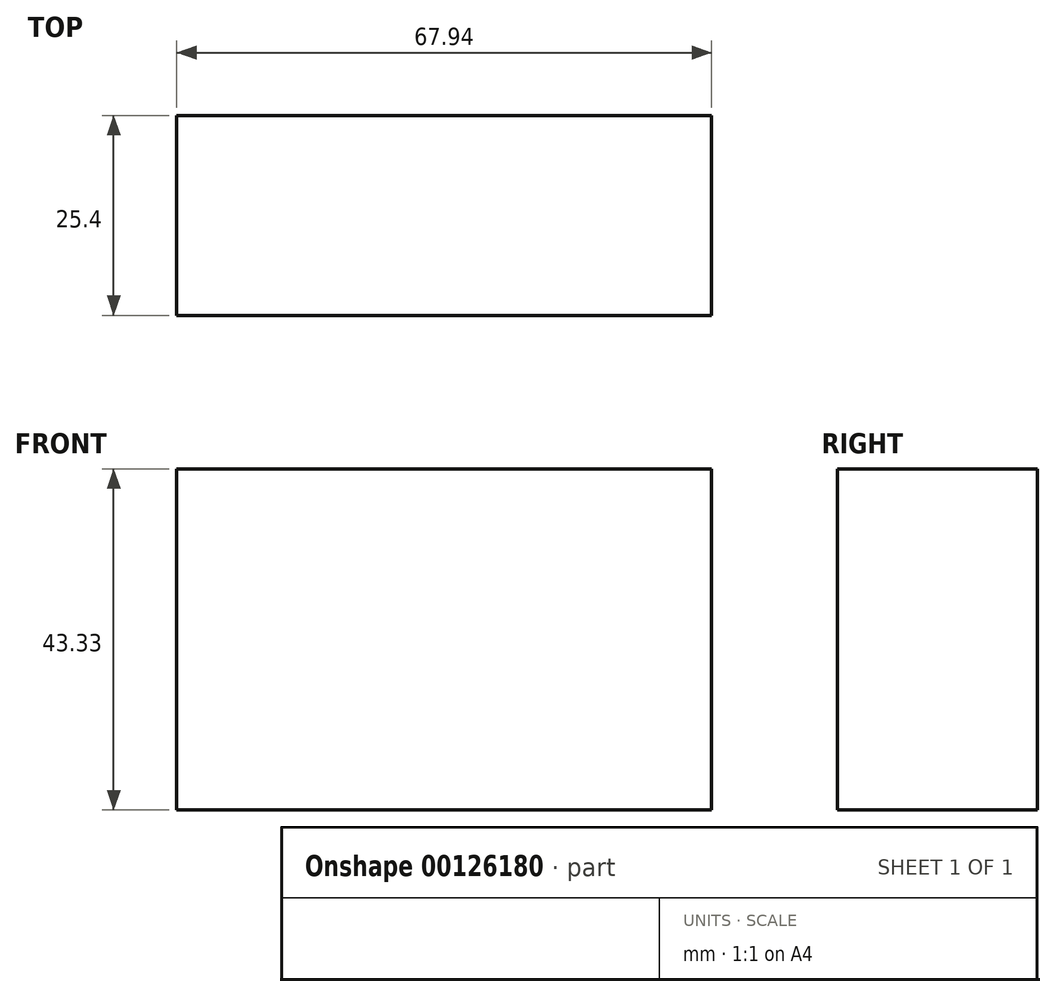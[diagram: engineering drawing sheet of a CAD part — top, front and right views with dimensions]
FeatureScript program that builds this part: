
annotation { "Feature Type Name" : "Feature", "Feature Type Description" : "" }
export const myFeature = defineFeature(function(context is Context, id is Id, definition is map)
    precondition{}
    {
        {
            var Q0;
            Q0=qCreatedBy(makeId("Front.planeOp"),FACE);
            var sketch = newSketch(context, id + "F0", { "sketchPlane" : qUnion([Q0])});
            skLineSegment(sketch, "E0.bottom", {"start": v(-32.22, 19.03) * mm, "end": v(35.72, 19.03) * mm});
            skLineSegment(sketch, "E0.top", {"start": v(-32.22, -24.3) * mm, "end": v(35.72, -24.3) * mm});
            skLineSegment(sketch, "E0.left", {"start": v(-32.22, 19.03) * mm, "end": v(-32.22, -24.3) * mm});
            skLineSegment(sketch, "E0.right", {"start": v(35.72, 19.03) * mm, "end": v(35.72, -24.3) * mm});
            skLineSegment(sketch, "E1.bottom", {"start": v(-213.51, -32.65) * mm, "end": v(-256.53, -32.65) * mm});
            skLineSegment(sketch, "E1.top", {"start": v(-213.51, 54.22) * mm, "end": v(-256.53, 54.22) * mm});
            skLineSegment(sketch, "E1.left", {"start": v(-213.51, -32.65) * mm, "end": v(-213.51, 54.22) * mm});
            skLineSegment(sketch, "E1.right", {"start": v(-256.53, -32.65) * mm, "end": v(-256.53, 54.22) * mm});
            skPoint(sketch, "E1.middle", {"position": v(-235.02, 10.79) * mm});
            skSolve(sketch);
        }
        {
            var Q0;
            Q0=makeQuery(id+"F0.imprint","IMPRINT",FACE,{"disambiguationData":[TD([[makeQuery(id+"F0.imprint","IMPRINT",EDGE,{"derivedFrom":sQuery(id+"F0.wireOp",EDGE,"E0.bottom")}),-1.0]])]});
            extrude(context, id + "F1", {"entities" : qUnion([Q0]), "depth" : 25.4 * mm, "offsetDistance" : 25.4 * mm});
        }
    });
